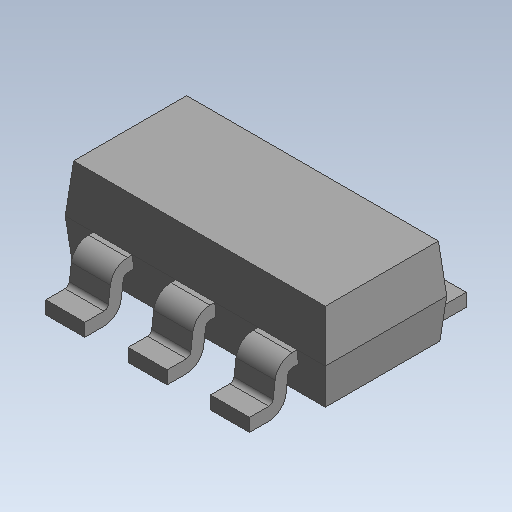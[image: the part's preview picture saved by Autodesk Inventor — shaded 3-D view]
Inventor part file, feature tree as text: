
AUTODESK INVENTOR PART (.ipt)
format: ipt  version: 2020 (Build 240168000, 168)  size: 107,520 bytes
history: native  units: mm (DEFAULTED — no unit token found)
features: fillet x1
ambient origin geometry x8: Origin, YZ Plane, XZ Plane, XY Plane, X Axis, Y Axis, Z Axis, Center Point
bodies: Solid1 (feature_tree)
feature tree (1):
  fillet  "Fillet2"  [1 undecoded]
note: 1 required parameter value undecoded (feature->parameter linkage not recoverable at this tier; creation-order binding heuristic only, values carry confidence <= 0.55)
